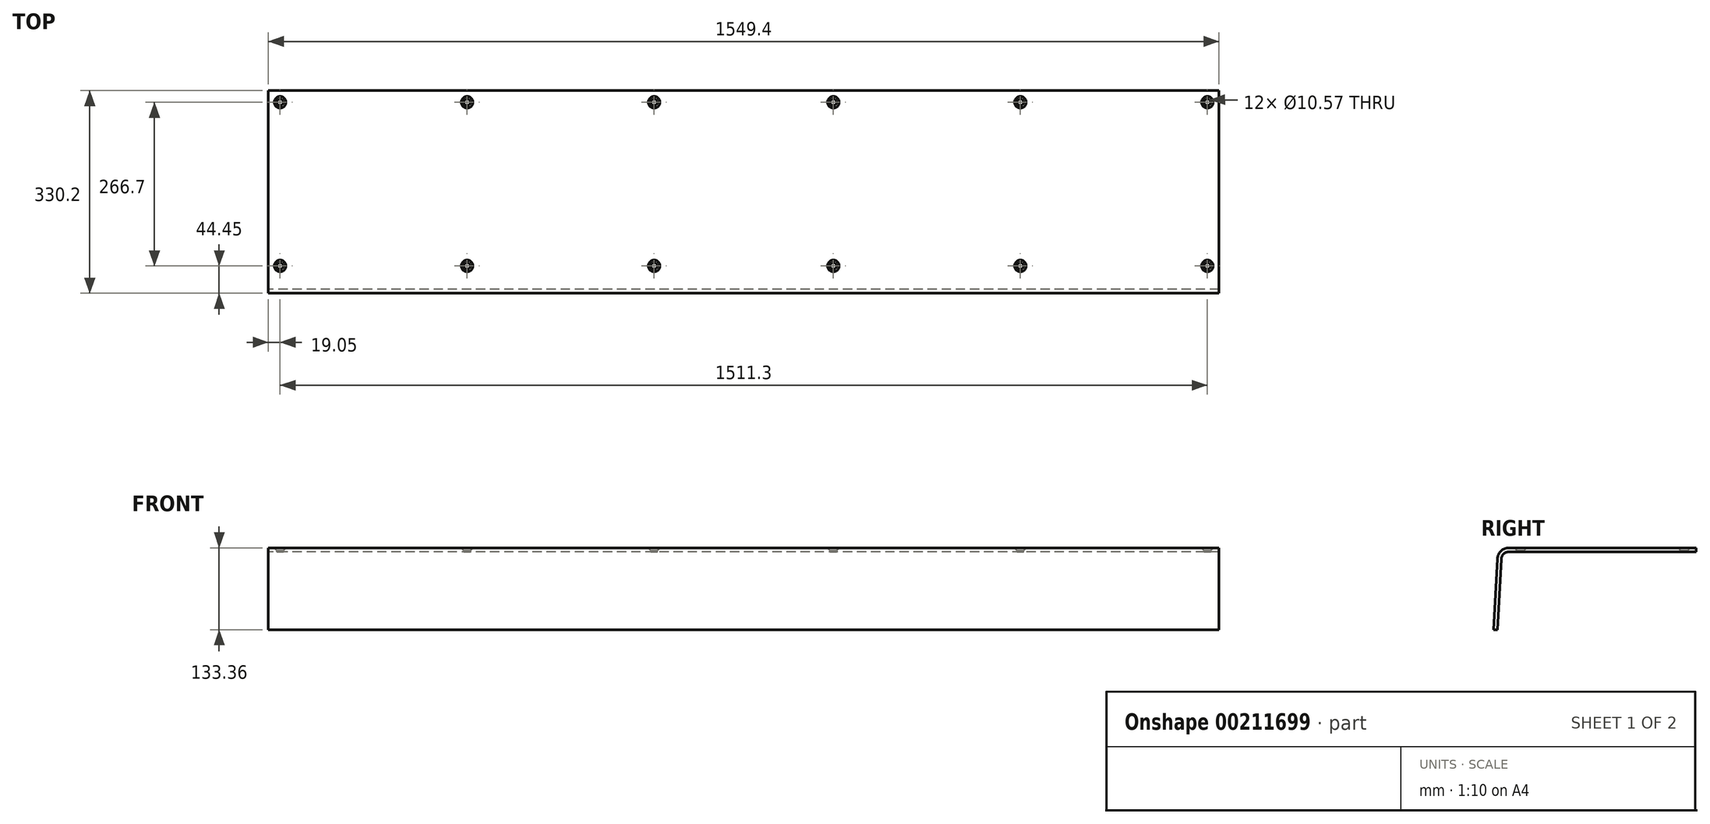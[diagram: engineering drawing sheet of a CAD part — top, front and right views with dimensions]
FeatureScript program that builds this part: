
annotation { "Feature Type Name" : "Feature", "Feature Type Description" : "" }
export const myFeature = defineFeature(function(context is Context, id is Id, definition is map)
    precondition{}
    {
        {
            var Q0;
            Q0=qCreatedBy(makeId("Right.planeOp"),FACE);
            var sketch = newSketch(context, id + "F0", { "sketchPlane" : qUnion([Q0])});
            skLineSegment(sketch, "E0", {"start": v(304.8, 0) * mm, "end": v(0, 0) * mm, "construction": true});
            skArc(sketch, "E1", {"start": v(0, 0) * mm, "mid": v(-10.91, -4.34) * mm, "end": v(-15.85, -15) * mm, "construction": true});
            skLineSegment(sketch, "E2", {"start": v(-15.85, -15) * mm, "end": v(-22.22, -130.18) * mm, "construction": true});
            skLineSegment(sketch, "E3.0", {"start": v(-19.02, -14.82) * mm, "end": v(-25.4, -130.18) * mm});
            skArc(sketch, "E3.1", {"start": v(0, 3.17) * mm, "mid": v(-13.1, -2.04) * mm, "end": v(-19.02, -14.82) * mm});
            skLineSegment(sketch, "E3.2", {"start": v(304.8, 3.18) * mm, "end": v(0, 3.18) * mm});
            skLineSegment(sketch, "E4", {"start": v(-22.22, -130.18) * mm, "end": v(-25.4, -130.18) * mm});
            skLineSegment(sketch, "E5", {"start": v(304.8, 3.18) * mm, "end": v(304.8, 0) * mm});
            skLineSegment(sketch, "E6.0", {"start": v(-12.68, -15.17) * mm, "end": v(-19.04, -130.18) * mm});
            skArc(sketch, "E6.1", {"start": v(0, -3.18) * mm, "mid": v(-8.73, -6.65) * mm, "end": v(-12.68, -15.17) * mm});
            skLineSegment(sketch, "E6.2", {"start": v(304.8, -3.18) * mm, "end": v(0, -3.18) * mm});
            skLineSegment(sketch, "E7", {"start": v(-22.22, -130.18) * mm, "end": v(-19.04, -130.18) * mm});
            skLineSegment(sketch, "E8", {"start": v(304.8, -3.18) * mm, "end": v(304.8, 0) * mm});
            skSolve(sketch);
        }
        {
            var Q0;
            Q0 = qSketchRegion(id + "F0", true);
            extrude(context, id + "F1", {"entities" : qUnion([Q0]), "depth" : 1549.4 * mm});
        }
        {
            var Q0;
            Q0=makeQuery(id+"F1.opExtrude","SWEPT_FACE",FACE,{"disambiguationData":[OSD([sQuery(id+"F0.wireOp",EDGE,"E3.2")])]});
            var sketch = newSketch(context, id + "F2", { "sketchPlane" : qUnion([Q0])});
            skPoint(sketch, "E9", {"position": v(19.05, 285.75) * mm});
            skPoint(sketch, "E10", {"position": v(323.85, 285.75) * mm});
            skPoint(sketch, "E11", {"position": v(628.65, 285.75) * mm});
            skPoint(sketch, "E12", {"position": v(1530.35, 285.75) * mm});
            skPoint(sketch, "E13", {"position": v(1225.55, 285.75) * mm});
            skPoint(sketch, "E14", {"position": v(920.75, 285.75) * mm});
            skLineSegment(sketch, "E15", {"start": v(82.3, 152.4) * mm, "end": v(575.4, 152.4) * mm, "construction": true});
            skPoint(sketch, "E16.MirrorP", {"position": v(19.05, 19.05) * mm});
            skPoint(sketch, "E17.MirrorP", {"position": v(323.85, 19.05) * mm});
            skPoint(sketch, "E18.MirrorP", {"position": v(628.65, 19.05) * mm});
            skPoint(sketch, "E19.MirrorP", {"position": v(920.75, 19.05) * mm});
            skPoint(sketch, "E20.MirrorP", {"position": v(1225.55, 19.05) * mm});
            skPoint(sketch, "E21.MirrorP", {"position": v(1530.35, 19.05) * mm});
            skSolve(sketch);
        }
        {
            var Q0;
            Q0=sQuery(id+"F2.wireOp",VERTEX,"E12");
            var Q1;
            Q1=sQuery(id+"F2.wireOp",VERTEX,"E21.MirrorP");
            var Q2;
            Q2=sQuery(id+"F2.wireOp",VERTEX,"E20.MirrorP");
            var Q3;
            Q3=sQuery(id+"F2.wireOp",VERTEX,"E13");
            var Q4;
            Q4=sQuery(id+"F2.wireOp",VERTEX,"E14");
            var Q5;
            Q5=sQuery(id+"F2.wireOp",VERTEX,"E19.MirrorP");
            var Q6;
            Q6=sQuery(id+"F2.wireOp",VERTEX,"E11");
            var Q7;
            Q7=sQuery(id+"F2.wireOp",VERTEX,"E18.MirrorP");
            var Q8;
            Q8=sQuery(id+"F2.wireOp",VERTEX,"E17.MirrorP");
            var Q9;
            Q9=sQuery(id+"F2.wireOp",VERTEX,"E10");
            var Q10;
            Q10=sQuery(id+"F2.wireOp",VERTEX,"E9");
            var Q11;
            Q11=sQuery(id+"F2.wireOp",VERTEX,"E16.MirrorP");
            var Q12;
            Q12=makeQuery(id+"F1.opExtrude","SWEPT_BODY",BODY,{"disambiguationData":[OSD([sQuery(id+"F0.wireOp",EDGE,"E3.0"),sQuery(id+"F0.wireOp",EDGE,"E3.1"),sQuery(id+"F0.wireOp",EDGE,"E3.2"),sQuery(id+"F0.wireOp",EDGE,"E4"),sQuery(id+"F0.wireOp",EDGE,"E5"),sQuery(id+"F0.wireOp",EDGE,"E6.0"),sQuery(id+"F0.wireOp",EDGE,"E6.1"),sQuery(id+"F0.wireOp",EDGE,"E6.2"),sQuery(id+"F0.wireOp",EDGE,"E7"),sQuery(id+"F0.wireOp",EDGE,"E8")])]});
            hole(context, id + "F3", {"style" : HoleStyle.C_SINK, "endStyle" : HoleEndStyle.BLIND, "holeDiameter" : 10.57 * mm, "cSinkDiameter" : 19.05 * mm, "cSinkAngle" : 82 * degree, "holeDepth" : 406.4 * mm, "startFromSketch" : true, "locations" : qUnion([Q0, Q1, Q2, Q3, Q4, Q5, Q6, Q7, Q8, Q9, Q10, Q11]), "scope" : qUnion([Q12])});
        }
    });
